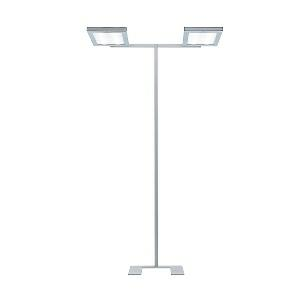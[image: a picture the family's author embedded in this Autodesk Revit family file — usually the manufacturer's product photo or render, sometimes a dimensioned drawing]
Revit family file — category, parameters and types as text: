
# Revit family: lavigo_-_dps_28000_vtl_r_g2_-twin-u_00810634_2b53
name_source: partatom
category: Lighting Fixtures
units: mm (PartAtom-declared; Revit-internal decimal feet)

## family parameters
Cut with Voids When Loaded = No
Host = Face
Light Source = No
Part Type = Normal
Room Calculation Point = No
Round Connector Dimension = Use Diameter
Shared = No

## types (1)
- LAVIGO - DPS 28000/VTL/R/G2 -TWIN-U (1 x LED VTL, 14250 lm, 3000-6500K)
    Apparent Load = 200 VA
    Approval mark = CE
    CIE Flux Codes = 60 87 97 12 100
    Color Rendering = 80-89
    Color Temperature = 3000-6500K
    Default Elevation = 1800 mm
    Description = DPS 28000/VTL/R/G2|Free-standing luminaire|light source: LED  3000-6500 K  Energy efficiency category A/A+/A++|work equipment: Electronic ballast|connected load: 220-240 V, 50/60 Hz|Power consumption: approx. 200 W|standby: approx. 0,50|power factor: approx. 0,966|luminous flux: 28500 lm|luminous efficacy: 142 lm/W|light distribution: Direct/indirect|direct ratio: approx. 12 %|color rendering index (CRI): >= 80|technology: Presence and daylight sensor control (PIR)|operation: Multi-function switch, Touch-LED|luminaire body|material: Steel/plastic|surface: Painted|colour: Silver metallic|lamp cover: Acrylic (PMMA), Satine|tubular section|material: Steel tube|surface: Painted|Form: Tubular section upright|colour of tubular section: Silver metallic|luminaire base|Form: C-form flat|weight (net): approx. 27.6 kg|mains lead: 3.00 m Mains plug CEE 7/VII|Fastening: Floor standing base|decorative contrast side parts: Flint grey|glare control: Prism aperture|luminance(L65): <= 3000 cd/m|unified glare rating(4H 8H): <=  16|special features: Luminaire head detachable, Direct light component with edge light and light-guide technology for homogenous light exit, Flicker-free, Integrated light and presence sensor PIR, Integrated light management for biodynamic light VTL, Retrofittable with TALK module, Separated, direct and indirect light individually adjustable|
    Frequency = 50 Hz, 60 Hz
    Height = 36 mm
    Lamp = 1 x LED VTL
    Lamp Light Flux = 14250 lm
    Lamp count = 1
    Length = 675 mm
    Luminous efficacy = 143 lm/W
    Manufacturer = Waldmann
    ModVariant = No
    Model = 00810634
    Mounting Place = Floor
    Mounting Type = Freestanding
    Number of Poles = 1
    OnlyDefault = Yes
    Power Factor = 1
    Product Name = LAVIGO - DPS 28000/VTL/R/G2 -TWIN-U
    Product group = Free standing luminaire
    ProductGroupID = 13
    Protection Class = Protection class I
    Protection Degree = IP 20
    RLX_Detail_Level = 1
    RLX_Emergency_Light_Flux = 0 lm
    RLX_Emergency_Type = 0
    RLX_Emergency_Type_DB = No
    RlxData = <blob elided: 36777 chars, md5=d7dfb914>
    Socket = socket
    Standby Power = 0 W
    System Light Flux = 28500 lm
    System Power = 200 W
    Type Comments = Product without accessories
    Type Image = 121714000-00642982.jpg
    URL = http://relux.com
    VarID = ---
    Voltage = 230 V
    Voltage Range = 220-240 V
    Weight = 0.00 kg
    Width = 350 mm

## geometry (parser evidence)
native form markers: Blend x4, Sweep x19
no freeform markers — native parametric forms only
